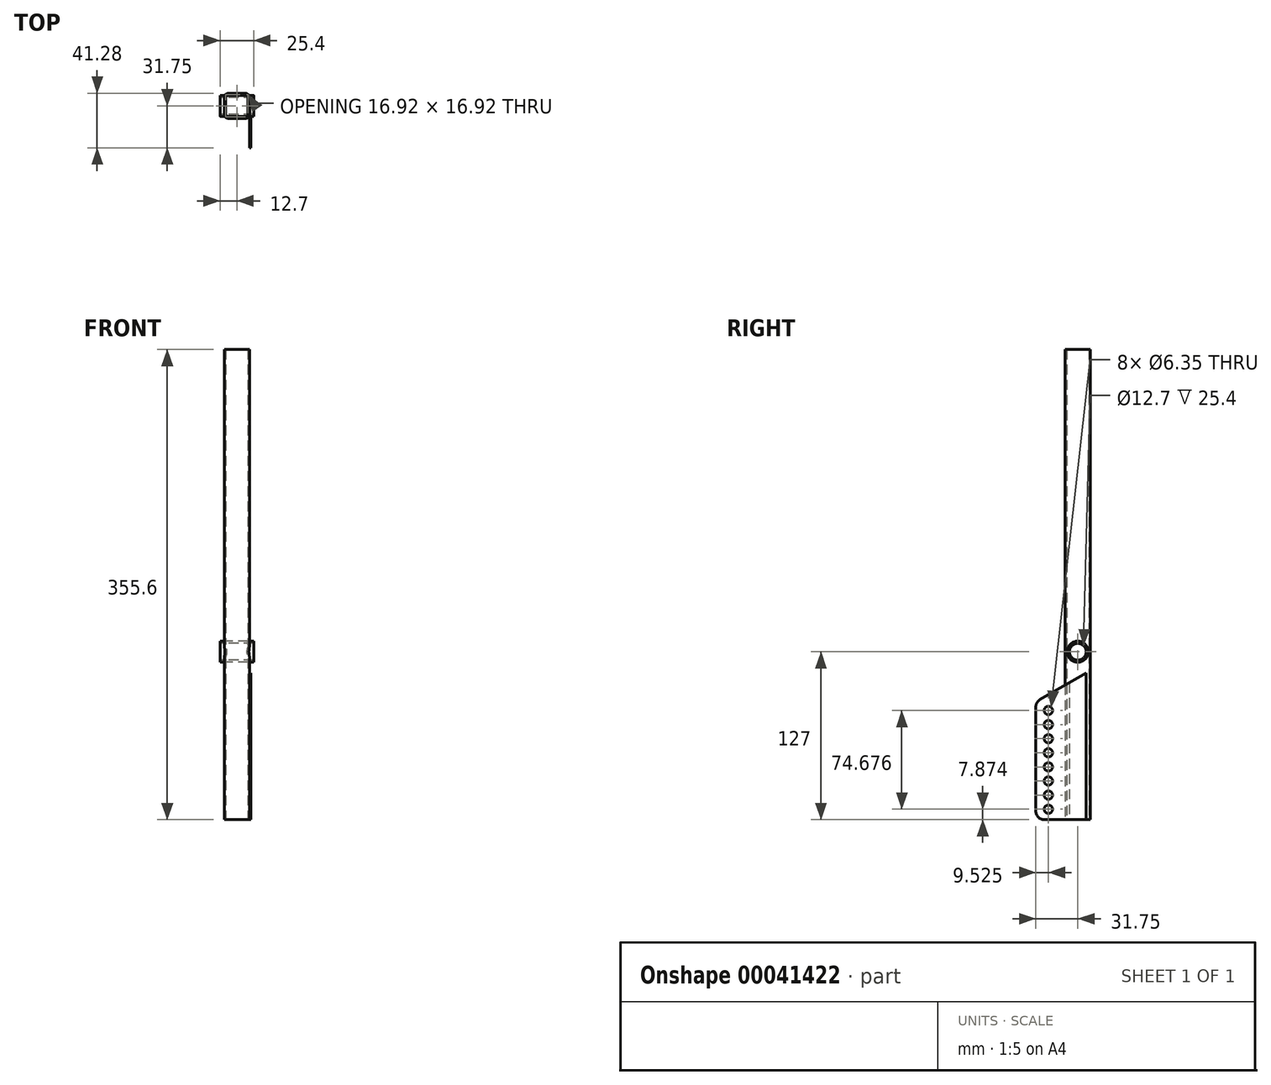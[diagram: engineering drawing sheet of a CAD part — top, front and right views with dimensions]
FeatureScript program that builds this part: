
annotation { "Feature Type Name" : "Feature", "Feature Type Description" : "" }
export const myFeature = defineFeature(function(context is Context, id is Id, definition is map)
    precondition{}
    {
        {
            var Q0;
            Q0=qCreatedBy(makeId("Top.planeOp"),FACE);
            var sketch = newSketch(context, id + "F0", { "sketchPlane" : qUnion([Q0])});
            skLineSegment(sketch, "E0.rect.bottom", {"start": v(6.35, -9.53) * mm, "end": v(-6.35, -9.53) * mm});
            skLineSegment(sketch, "E0.rect.top", {"start": v(6.35, 9.52) * mm, "end": v(-6.35, 9.52) * mm});
            skLineSegment(sketch, "E0.rect.left", {"start": v(9.53, -6.35) * mm, "end": v(9.53, 6.35) * mm});
            skLineSegment(sketch, "E0.rect.right", {"start": v(-9.53, -6.35) * mm, "end": v(-9.53, 6.35) * mm});
            skPoint(sketch, "E0.rect.middle", {"position": v(0, 0) * mm});
            skPoint(sketch, "E1.visualSharp", {"position": v(-9.53, 9.52) * mm});
            skArc(sketch, "E1.filletArc", {"start": v(-6.35, 9.52) * mm, "mid": v(-8.6, 8.6) * mm, "end": v(-9.52, 6.35) * mm});
            skPoint(sketch, "E2.visualSharp", {"position": v(9.53, 9.52) * mm});
            skArc(sketch, "E2.filletArc", {"start": v(9.52, 6.35) * mm, "mid": v(8.6, 8.6) * mm, "end": v(6.35, 9.52) * mm});
            skPoint(sketch, "E3.visualSharp", {"position": v(9.53, -9.53) * mm});
            skArc(sketch, "E3.filletArc", {"start": v(6.35, -9.53) * mm, "mid": v(8.6, -8.6) * mm, "end": v(9.52, -6.35) * mm});
            skPoint(sketch, "E4.visualSharp", {"position": v(-9.52, -9.53) * mm});
            skArc(sketch, "E4.filletArc", {"start": v(-9.52, -6.35) * mm, "mid": v(-8.6, -8.6) * mm, "end": v(-6.35, -9.52) * mm});
            skLineSegment(sketch, "E5.0", {"start": v(-8.46, -5.92) * mm, "end": v(-8.46, 5.92) * mm});
            skLineSegment(sketch, "E5.1", {"start": v(5.92, -8.46) * mm, "end": v(-5.92, -8.46) * mm});
            skLineSegment(sketch, "E5.2", {"start": v(8.46, -5.92) * mm, "end": v(8.46, 5.92) * mm});
            skLineSegment(sketch, "E5.3", {"start": v(5.92, 8.46) * mm, "end": v(-5.92, 8.46) * mm});
            skPoint(sketch, "E6.visualSharp", {"position": v(8.46, 8.46) * mm});
            skArc(sketch, "E6.filletArc", {"start": v(8.46, 5.92) * mm, "mid": v(7.71, 7.71) * mm, "end": v(5.92, 8.46) * mm});
            skPoint(sketch, "E7.visualSharp", {"position": v(-8.46, 8.46) * mm});
            skArc(sketch, "E7.filletArc", {"start": v(-5.92, 8.46) * mm, "mid": v(-7.71, 7.71) * mm, "end": v(-8.46, 5.92) * mm});
            skPoint(sketch, "E8.visualSharp", {"position": v(-8.46, -8.46) * mm});
            skArc(sketch, "E8.filletArc", {"start": v(-8.46, -5.92) * mm, "mid": v(-7.71, -7.71) * mm, "end": v(-5.92, -8.46) * mm});
            skPoint(sketch, "E9.visualSharp", {"position": v(8.46, -8.46) * mm});
            skArc(sketch, "E9.filletArc", {"start": v(5.92, -8.46) * mm, "mid": v(7.71, -7.71) * mm, "end": v(8.46, -5.92) * mm});
            skSolve(sketch);
        }
        {
            var Q0;
            Q0=makeQuery(id+"F0.imprint","IMPRINT",FACE,{"disambiguationData":[TD([[makeQuery(id+"F0.imprint","IMPRINT",EDGE,{"derivedFrom":sQuery(id+"F0.wireOp",EDGE,"E0.rect.bottom")}),-1.0]])]});
            extrude(context, id + "F1", {"entities" : qUnion([Q0]), "depth" : 355.6 * mm});
        }
        {
            var Q0;
            Q0=makeQuery(id+"F1.opExtrude","SWEPT_FACE",FACE,{"disambiguationData":[OSD([sQuery(id+"F0.wireOp",EDGE,"E0.rect.left")])]});
            var sketch = newSketch(context, id + "F2", { "sketchPlane" : qUnion([Q0])});
            skCircle(sketch, "E10", {"center": v(0, 127) * mm, "radius": 7.94 * mm});
            skLineSegment(sketch, "E11", {"start": v(0, 355.6) * mm, "end": v(0, 26.5) * mm, "construction": true});
            skSolve(sketch);
        }
        {
            var Q0;
            {var subQ0=sQuery(id+"F0.wireOp",EDGE,"E0.rect.left");var subQ2=sQuery(id+"F2.wireOp",EDGE,"E10");var subQ5=makeQuery(id+"F1.opExtrude","SWEPT_EDGE",EDGE,{"disambiguationData":[OSD([subQ0,sQuery(id+"F0.wireOp",EDGE,"E3.filletArc")])]});var subQ7=makeQuery(id+"F2.imprint","INTERSECT",VERTEX,{"disambiguationData":[OD(0.0)],"derivedFrom":[subQ5,subQ2]});Q0=makeQuery(id+"F2.imprint","IMPRINT",FACE,{"disambiguationData":[TD([[makeQuery(id+"F2.imprint","IMPRINT",EDGE,{"disambiguationData":[TD([[subQ7,1.0]])],"derivedFrom":subQ2}),1.0]])]});}
            var Q1;
            {var subQ0=makeQuery(id+"F1.opExtrude","SWEPT_EDGE",EDGE,{"disambiguationData":[OSD([sQuery(id+"F0.wireOp",EDGE,"E0.rect.left"),sQuery(id+"F0.wireOp",EDGE,"E2.filletArc")])]});var subQ1=sQuery(id+"F2.wireOp",EDGE,"E10");var subQ3=makeQuery(id+"F2.imprint","INTERSECT",VERTEX,{"disambiguationData":[OD(0.0)],"derivedFrom":[subQ0,subQ1]});Q1=makeQuery(id+"F2.imprint","IMPRINT",FACE,{"disambiguationData":[TD([[makeQuery(id+"F2.imprint","IMPRINT",EDGE,{"disambiguationData":[TD([[subQ3,1.0]])],"derivedFrom":subQ1}),1.0]])]});}
            var Q2;
            {var subQ0=makeQuery(id+"F1.opExtrude","SWEPT_EDGE",EDGE,{"disambiguationData":[OSD([sQuery(id+"F0.wireOp",EDGE,"E0.rect.left"),sQuery(id+"F0.wireOp",EDGE,"E3.filletArc")])]});var subQ1=sQuery(id+"F2.wireOp",EDGE,"E10");var subQ3=makeQuery(id+"F2.imprint","INTERSECT",VERTEX,{"disambiguationData":[OD(0.0)],"derivedFrom":[subQ0,subQ1]});Q2=makeQuery(id+"F2.imprint","IMPRINT",FACE,{"disambiguationData":[TD([[makeQuery(id+"F2.imprint","IMPRINT",EDGE,{"disambiguationData":[TD([[subQ3,-1.0]])],"derivedFrom":subQ1}),1.0]])]});}
            extrude(context, id + "F3", {"entities" : qUnion([Q0, Q1, Q2]), "operationType" : NewBodyOperationType.REMOVE, "endBound" : BoundingType.THROUGH_ALL, "oppositeDirection" : true, "depth" : 25.4 * mm});
        }
        {
            var Q0;
            {var subQ0=sQuery(id+"F0.wireOp",EDGE,"E0.rect.left");var subQ1=sQuery(id+"F0.wireOp",EDGE,"E3.filletArc");var subQ2=sQuery(id+"F0.wireOp",EDGE,"E2.filletArc");Q0=makeQuery(id+"F3.boolean.opBoolean","SPLIT",FACE,{"disambiguationData":[TD([makeQuery(id+"F1.opExtrude","CAP_FACE",FACE,{"disambiguationData":[OSD([sQuery(id+"F0.wireOp",EDGE,"E0.rect.bottom"),sQuery(id+"F0.wireOp",EDGE,"E0.rect.top"),subQ0,sQuery(id+"F0.wireOp",EDGE,"E0.rect.right"),sQuery(id+"F0.wireOp",EDGE,"E1.filletArc"),subQ2,subQ1,sQuery(id+"F0.wireOp",EDGE,"E4.filletArc"),sQuery(id+"F0.wireOp",EDGE,"E5.0"),sQuery(id+"F0.wireOp",EDGE,"E5.1"),sQuery(id+"F0.wireOp",EDGE,"E5.2"),sQuery(id+"F0.wireOp",EDGE,"E5.3"),sQuery(id+"F0.wireOp",EDGE,"E6.filletArc"),sQuery(id+"F0.wireOp",EDGE,"E7.filletArc"),sQuery(id+"F0.wireOp",EDGE,"E8.filletArc"),sQuery(id+"F0.wireOp",EDGE,"E9.filletArc")])],"isStart":true})])],"derivedFrom":makeQuery(id+"F1.opExtrude","SWEPT_FACE",FACE,{"disambiguationData":[OSD([subQ0])]})});}
            var sketch = newSketch(context, id + "F4", { "sketchPlane" : qUnion([Q0])});
            skCircle(sketch, "E12", {"center": v(0, 127) * mm, "radius": 7.94 * mm});
            skCircle(sketch, "E13", {"center": v(0, 127) * mm, "radius": 6.35 * mm});
            skSolve(sketch);
        }
        {
            var Q0;
            Q0 = qSketchRegion(id + "F4", true);
            extrude(context, id + "F5", {"entities" : qUnion([Q0]), "operationType" : NewBodyOperationType.ADD, "depth" : 3.17 * mm, "hasSecondDirection" : true, "secondDirectionOppositeDirection" : true, "secondDirectionDepth" : 22.22 * mm});
        }
        {
            var Q0;
            {var subQ0=sQuery(id+"F0.wireOp",EDGE,"E0.rect.left");var subQ1=sQuery(id+"F0.wireOp",EDGE,"E3.filletArc");var subQ2=sQuery(id+"F0.wireOp",EDGE,"E2.filletArc");Q0=makeQuery(id+"F3.boolean.opBoolean","SPLIT",FACE,{"disambiguationData":[TD([makeQuery(id+"F1.opExtrude","CAP_FACE",FACE,{"disambiguationData":[OSD([sQuery(id+"F0.wireOp",EDGE,"E0.rect.bottom"),sQuery(id+"F0.wireOp",EDGE,"E0.rect.top"),subQ0,sQuery(id+"F0.wireOp",EDGE,"E0.rect.right"),sQuery(id+"F0.wireOp",EDGE,"E1.filletArc"),subQ2,subQ1,sQuery(id+"F0.wireOp",EDGE,"E4.filletArc"),sQuery(id+"F0.wireOp",EDGE,"E5.0"),sQuery(id+"F0.wireOp",EDGE,"E5.1"),sQuery(id+"F0.wireOp",EDGE,"E5.2"),sQuery(id+"F0.wireOp",EDGE,"E5.3"),sQuery(id+"F0.wireOp",EDGE,"E6.filletArc"),sQuery(id+"F0.wireOp",EDGE,"E7.filletArc"),sQuery(id+"F0.wireOp",EDGE,"E8.filletArc"),sQuery(id+"F0.wireOp",EDGE,"E9.filletArc")])],"isStart":true})])],"derivedFrom":makeQuery(id+"F1.opExtrude","SWEPT_FACE",FACE,{"disambiguationData":[OSD([subQ0])]})});}
            var sketch = newSketch(context, id + "F6", { "sketchPlane" : qUnion([Q0])});
            skLineSegment(sketch, "E14", {"start": v(6.35, 0) * mm, "end": v(-25.4, 0) * mm});
            skLineSegment(sketch, "E15", {"start": v(-31.75, 6.35) * mm, "end": v(-31.75, 85.23) * mm});
            skLineSegment(sketch, "E16", {"start": v(-28.58, 90.73) * mm, "end": v(6.35, 110.9) * mm});
            skLineSegment(sketch, "E17", {"start": v(6.35, 110.9) * mm, "end": v(6.35, 0) * mm});
            skLineSegment(sketch, "E18", {"start": v(-22.23, 121.45) * mm, "end": v(-22.23, -14.67) * mm, "construction": true});
            skCircle(sketch, "E19", {"center": v(-22.23, 82.55) * mm, "radius": 3.18 * mm});
            skCircle(sketch, "E20.0.1.0", {"center": v(-22.23, 71.88) * mm, "radius": 3.18 * mm});
            skCircle(sketch, "E20.0.2.0", {"center": v(-22.23, 61.21) * mm, "radius": 3.18 * mm});
            skCircle(sketch, "E20.0.3.0", {"center": v(-22.23, 50.55) * mm, "radius": 3.18 * mm});
            skCircle(sketch, "E20.0.4.0", {"center": v(-22.23, 39.88) * mm, "radius": 3.18 * mm});
            skCircle(sketch, "E20.0.5.0", {"center": v(-22.23, 29.21) * mm, "radius": 3.18 * mm});
            skCircle(sketch, "E20.0.6.0", {"center": v(-22.23, 18.54) * mm, "radius": 3.18 * mm});
            skCircle(sketch, "E20.0.7.0", {"center": v(-22.23, 7.87) * mm, "radius": 3.18 * mm});
            skLineSegment(sketch, "E20.direction1", {"start": v(-22.23, 82.55) * mm, "end": v(3.17, 82.55) * mm, "construction": true});
            skLineSegment(sketch, "E20.direction2", {"start": v(-22.23, 82.55) * mm, "end": v(-22.23, 71.88) * mm, "construction": true});
            skPoint(sketch, "E21.visualSharp", {"position": v(-31.75, 88.9) * mm});
            skArc(sketch, "E21.filletArc", {"start": v(-28.58, 90.73) * mm, "mid": v(-30.9, 88.4) * mm, "end": v(-31.75, 85.23) * mm});
            skPoint(sketch, "E22.visualSharp", {"position": v(-31.75, 0) * mm});
            skArc(sketch, "E22.filletArc", {"start": v(-31.75, 6.35) * mm, "mid": v(-29.9, 1.86) * mm, "end": v(-25.4, 0) * mm});
            skSolve(sketch);
        }
        {
            var Q0;
            {var subQ5=sQuery(id+"F6.wireOp",EDGE,"E15");Q0=makeQuery(id+"F6.imprint","IMPRINT",FACE,{"disambiguationData":[TD([[makeQuery(id+"F6.imprint","IMPRINT",EDGE,{"derivedFrom":subQ5}),-1.0]])]});}
            var Q1;
            {var subQ11=sQuery(id+"F6.wireOp",EDGE,"E17");Q1=makeQuery(id+"F6.imprint","IMPRINT",FACE,{"disambiguationData":[TD([[makeQuery(id+"F6.imprint","IMPRINT",EDGE,{"derivedFrom":subQ11}),-1.0]])]});}
            extrude(context, id + "F7", {"entities" : qUnion([Q0, Q1]), "operationType" : NewBodyOperationType.ADD, "depth" : 1.07 * mm});
        }
    });
